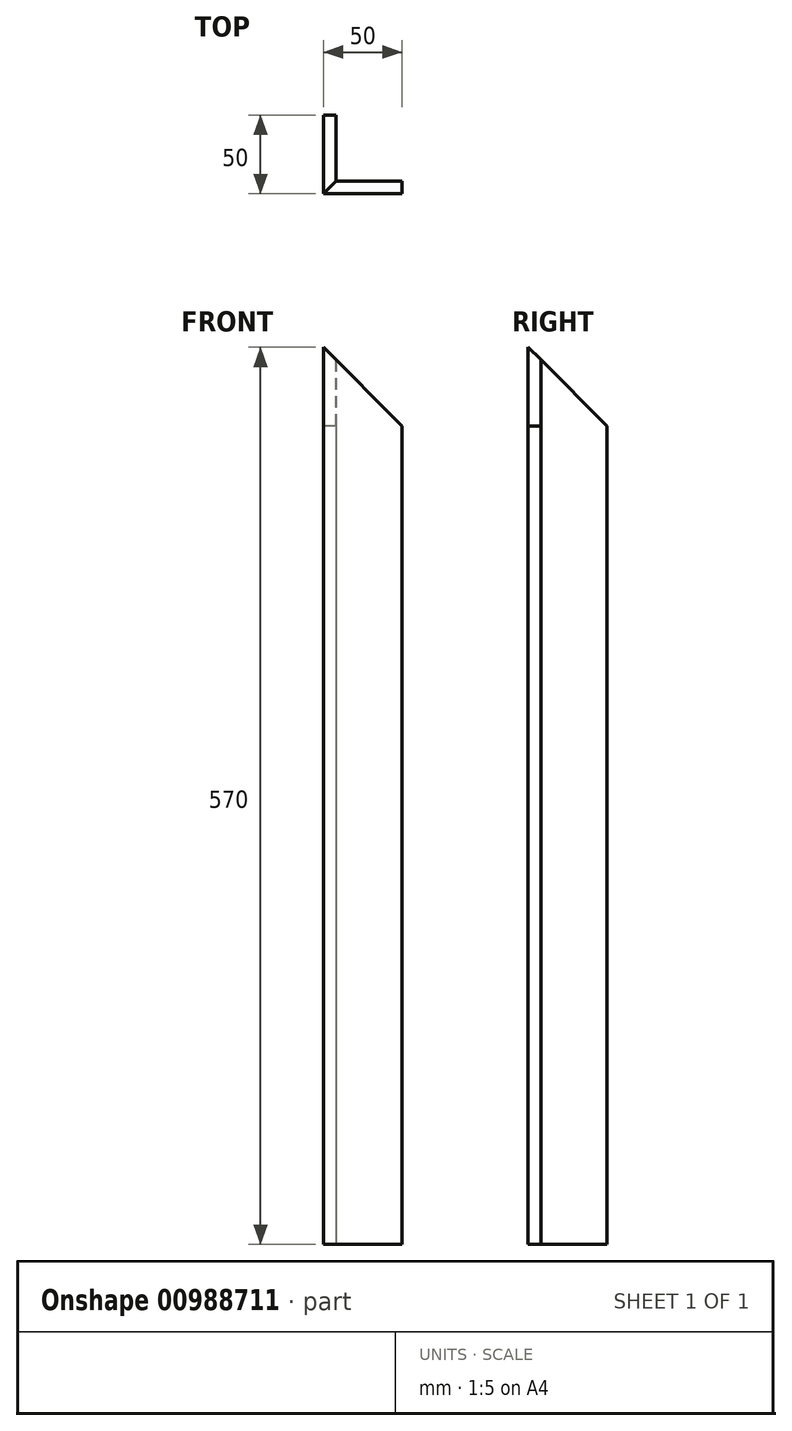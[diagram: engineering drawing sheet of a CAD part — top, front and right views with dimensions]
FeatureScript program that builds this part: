
annotation { "Feature Type Name" : "Feature", "Feature Type Description" : "" }
export const myFeature = defineFeature(function(context is Context, id is Id, definition is map)
    precondition{}
    {
        {
            var Q0;
            Q0=qCreatedBy(makeId("Top.planeOp"),FACE);
            var sketch = newSketch(context, id + "F0", { "sketchPlane" : qUnion([Q0])});
            skLineSegment(sketch, "E0", {"start": v(0, 0) * mm, "end": v(0, 50) * mm});
            skLineSegment(sketch, "E1", {"start": v(0, 50) * mm, "end": v(8, 50) * mm});
            skLineSegment(sketch, "E2", {"start": v(8, 50) * mm, "end": v(8, 8) * mm});
            skLineSegment(sketch, "E3", {"start": v(8, 8) * mm, "end": v(50, 8) * mm});
            skLineSegment(sketch, "E4", {"start": v(50, 8) * mm, "end": v(50, 0) * mm});
            skLineSegment(sketch, "E5", {"start": v(50, 0) * mm, "end": v(0, 0) * mm});
            skSolve(sketch);
        }
        {
            var Q0;
            Q0 = qSketchRegion(id + "F0", true);
            extrude(context, id + "F1", {"entities" : qUnion([Q0]), "depth" : 570 * mm, "offsetDistance" : 25 * mm});
        }
        {
            var Q0;
            Q0=makeQuery(id+"F1.opExtrude","SWEPT_FACE",FACE,{"disambiguationData":[OSD([sQuery(id+"F0.wireOp",EDGE,"E5")])]});
            var sketch = newSketch(context, id + "F2", { "sketchPlane" : qUnion([Q0])});
            skLineSegment(sketch, "E6", {"start": v(0, 570) * mm, "end": v(50, 520) * mm});
            skLineSegment(sketch, "E7", {"start": v(50, 520) * mm, "end": v(50, 570) * mm});
            skLineSegment(sketch, "E8", {"start": v(50, 570) * mm, "end": v(0, 570) * mm});
            skSolve(sketch);
        }
        {
            var Q0;
            Q0=makeQuery(id+"F2.imprint","IMPRINT",FACE,{"disambiguationData":[TD([[makeQuery(id+"F2.imprint","IMPRINT",EDGE,{"derivedFrom":sQuery(id+"F2.wireOp",EDGE,"E6")}),1.0]])]});
            var Q1;
            Q1=makeQuery(id+"F1.opExtrude","SWEPT_FACE",FACE,{"disambiguationData":[OSD([sQuery(id+"F0.wireOp",EDGE,"E3")])]});
            extrude(context, id + "F3", {"entities" : qUnion([Q0]), "operationType" : NewBodyOperationType.REMOVE, "endBound" : BoundingType.UP_TO_SURFACE, "oppositeDirection" : true, "depth" : 25 * mm, "endBoundEntityFace" : qUnion([Q1]), "offsetDistance" : 25 * mm});
        }
        {
            var Q0;
            Q0=makeQuery(id+"F1.opExtrude","SWEPT_FACE",FACE,{"disambiguationData":[OSD([sQuery(id+"F0.wireOp",EDGE,"E0")])]});
            var sketch = newSketch(context, id + "F4", { "sketchPlane" : qUnion([Q0])});
            skLineSegment(sketch, "E9", {"start": v(0, 570) * mm, "end": v(0, 520) * mm});
            skLineSegment(sketch, "E10", {"start": v(0, 520) * mm, "end": v(-50, 520) * mm});
            skLineSegment(sketch, "E11", {"start": v(-50, 520) * mm, "end": v(0, 570) * mm});
            skSolve(sketch);
        }
        {
            var Q0;
            {var subQ0=sQuery(id+"F4.wireOp",EDGE,"E11");Q0=makeQuery(id+"F4.imprint","IMPRINT",FACE,{"disambiguationData":[TD([[makeQuery(id+"F4.imprint","IMPRINT",EDGE,{"derivedFrom":subQ0}),1.0]])]});}
            var Q1;
            Q1=makeQuery(id+"F1.opExtrude","SWEPT_FACE",FACE,{"disambiguationData":[OSD([sQuery(id+"F0.wireOp",EDGE,"E2")])]});
            extrude(context, id + "F5", {"entities" : qUnion([Q0]), "operationType" : NewBodyOperationType.REMOVE, "endBound" : BoundingType.UP_TO_SURFACE, "oppositeDirection" : true, "depth" : 25 * mm, "endBoundEntityFace" : qUnion([Q1]), "offsetDistance" : 25 * mm});
        }
    });
